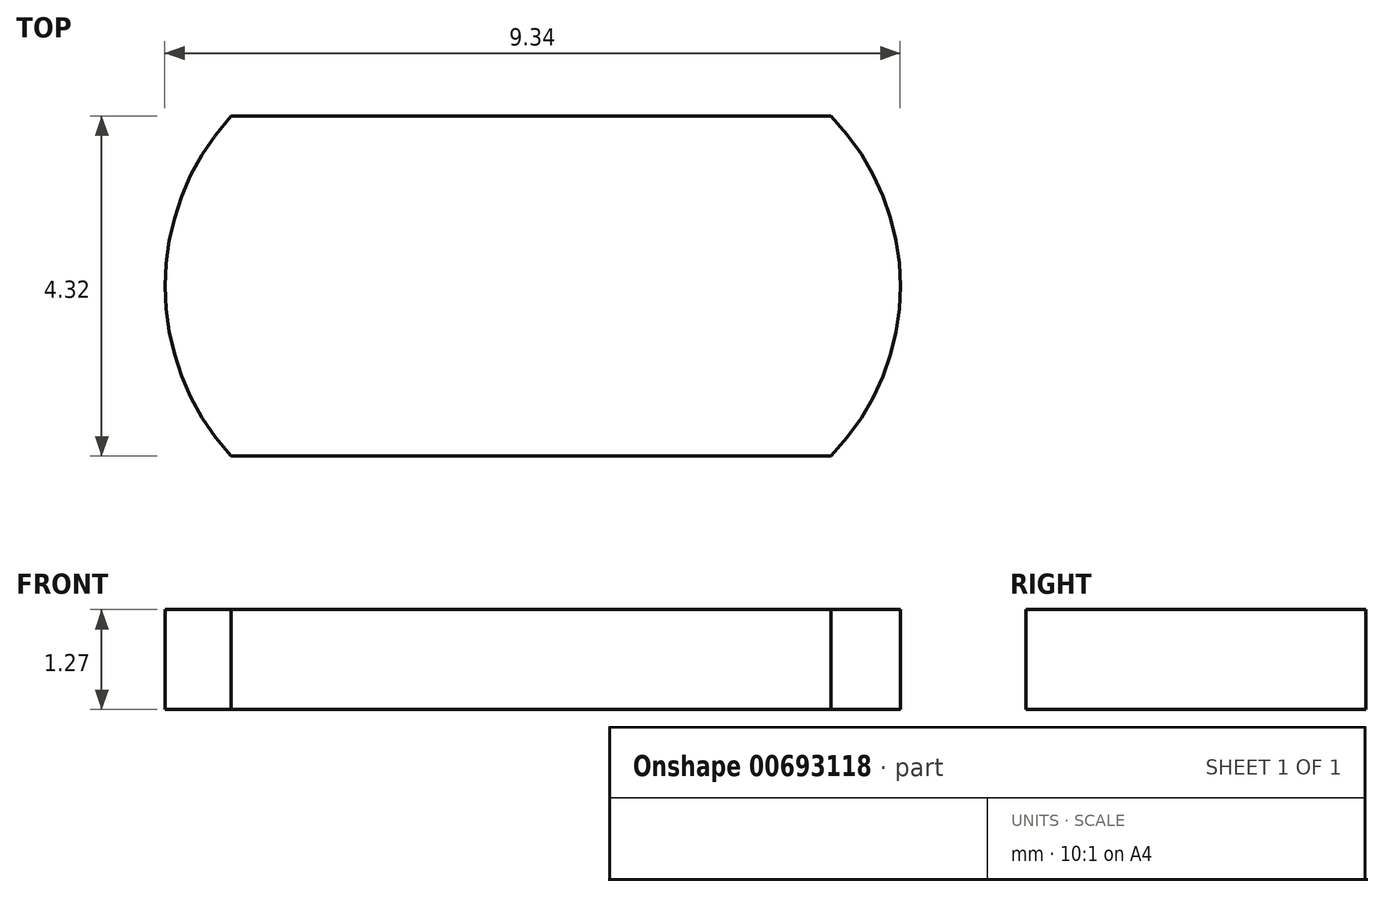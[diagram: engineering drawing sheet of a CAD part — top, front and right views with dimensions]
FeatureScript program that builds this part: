
annotation { "Feature Type Name" : "Feature", "Feature Type Description" : "" }
export const myFeature = defineFeature(function(context is Context, id is Id, definition is map)
    precondition{}
    {
        {
            var Q0;
            Q0=qCreatedBy(makeId("Top.planeOp"),FACE);
            var sketch = newSketch(context, id + "F0", { "sketchPlane" : qUnion([Q0])});
            skLineSegment(sketch, "E0.bottom", {"start": v(0, 0) * mm, "end": v(-7.62, 0) * mm});
            skLineSegment(sketch, "E0.top", {"start": v(0, 4.32) * mm, "end": v(-7.62, 4.32) * mm});
            skArc(sketch, "E1", {"start": v(0, 0) * mm, "mid": v(0.88, 2.16) * mm, "end": v(0, 4.32) * mm});
            skArc(sketch, "E2", {"start": v(-7.62, 4.32) * mm, "mid": v(-8.46, 2.16) * mm, "end": v(-7.62, 0) * mm});
            skSolve(sketch);
        }
        {
            var Q0;
            Q0=makeQuery(id+"F0.imprint","IMPRINT",FACE,{"disambiguationData":[TD([[makeQuery(id+"F0.imprint","IMPRINT",EDGE,{"derivedFrom":sQuery(id+"F0.wireOp",EDGE,"E0.bottom")}),-1.0]])]});
            extrude(context, id + "F1", {"entities" : qUnion([Q0]), "depth" : 1.27 * mm});
        }
    });
